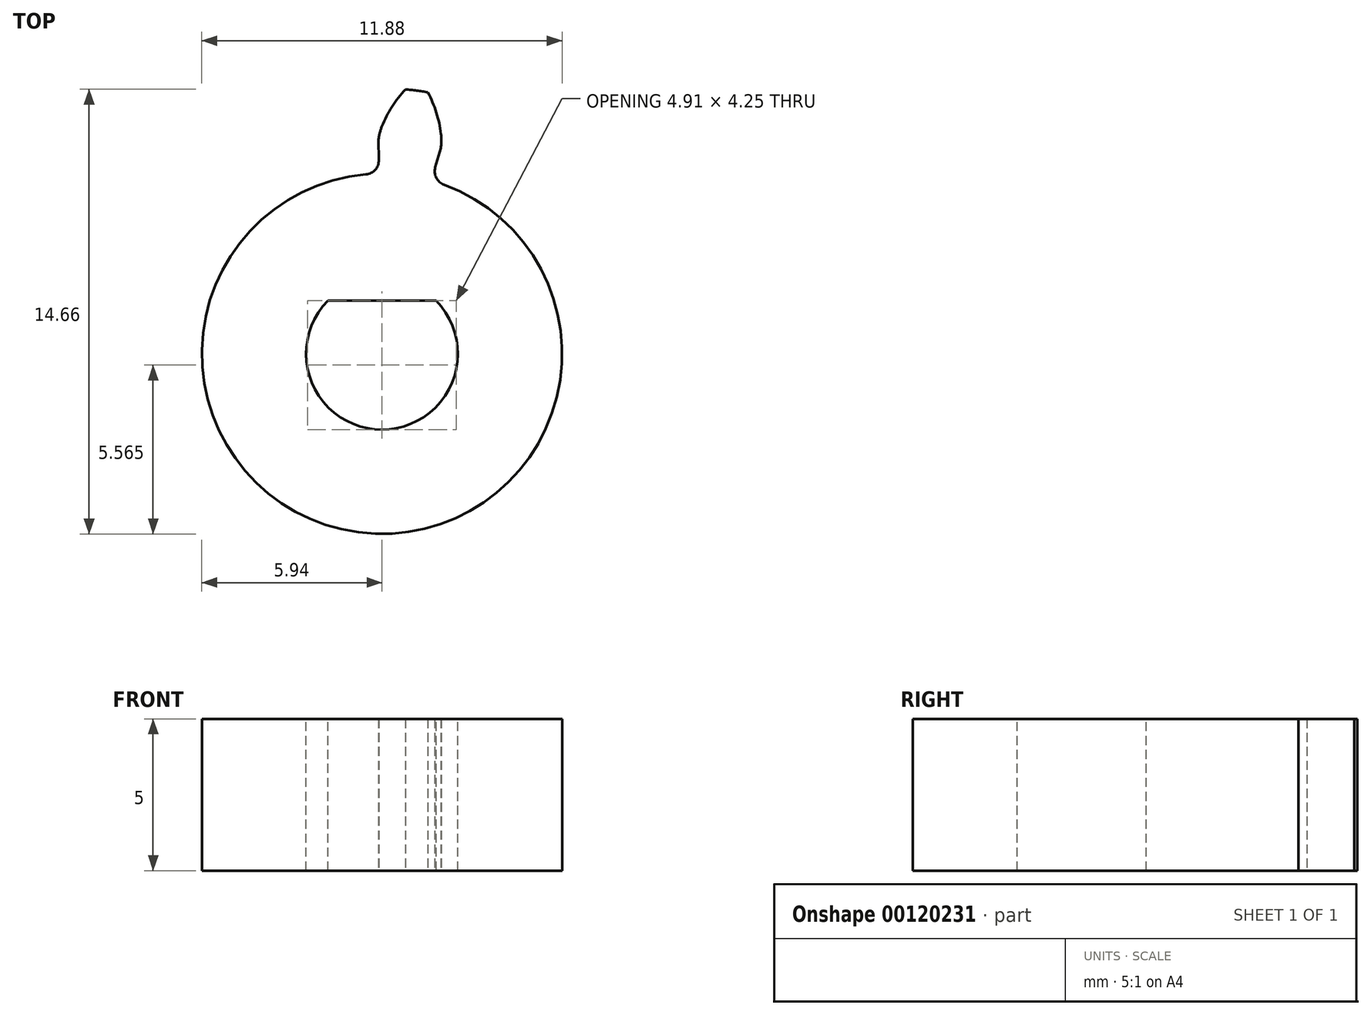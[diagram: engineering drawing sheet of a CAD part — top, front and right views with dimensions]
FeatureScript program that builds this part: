
annotation { "Feature Type Name" : "Feature", "Feature Type Description" : "" }
export const myFeature = defineFeature(function(context is Context, id is Id, definition is map)
    precondition{}
    {
        {
            var Q0;
            Q0=qCreatedBy(makeId("Front.planeOp"),FACE);
            var sketch = newSketch(context, id + "F0", { "sketchPlane" : qUnion([Q0])});
            skLineSegment(sketch, "E0", {"start": v(0, 72.27) * mm, "end": v(0, -50.25) * mm, "construction": true});
            skSolve(sketch);
        }
        {
            var Q0;
            Q0=qCreatedBy(makeId("Top.planeOp"),FACE);
            var sketch = newSketch(context, id + "F1", { "sketchPlane" : qUnion([Q0])});
            skCircle(sketch, "E1", {"center": v(0, 0) * mm, "radius": 7.5 * mm, "construction": true});
            skCircle(sketch, "E2", {"center": v(0, 0) * mm, "radius": 5.94 * mm});
            skSolve(sketch);
        }
        {
            var Q0;
            Q0=qSketchRegion(id+"F1",true);
            extrude(context, id + "F2", {"entities" : qUnion([Q0]), "depth" : 5 * mm});
        }
        {
            var Q0;
            Q0=makeQuery(id+"F2.opExtrude","CAP_FACE",FACE,{"disambiguationData":[OSD([sQuery(id+"F1.wireOp",EDGE,"E2"),sQuery(id+"F1.wireOp",EDGE,"lKhcHiEn-qWT4-b5GR-9CCX-N4hY3lJjeW35"),sQuery(id+"F1.wireOp",EDGE,"zsuhm7zz-1LAn-hH0Z-Fbhr-HMJ1RvOiH2OX")])],"isStart":false});
            var sketch = newSketch(context, id + "F3", { "sketchPlane" : qUnion([Q0])});
            skArc(sketch, "E3", {"start": v(-1.79, 1.75) * mm, "mid": v(0, -2.5) * mm, "end": v(1.79, 1.75) * mm});
            skLineSegment(sketch, "E4", {"start": v(-1.79, 1.75) * mm, "end": v(1.79, 1.75) * mm});
            skPoint(sketch, "E5", {"position": v(0, 2.5) * mm});
            skArc(sketch, "E6", {"start": v(-1.79, 1.75) * mm, "mid": v(0, 2.5) * mm, "end": v(1.79, 1.75) * mm, "construction": true});
            skSolve(sketch);
        }
        {
            var Q0;
            Q0 = qSketchRegion(id + "F3", true);
            extrude(context, id + "F4", {"entities" : qUnion([Q0]), "operationType" : NewBodyOperationType.REMOVE, "endBound" : BoundingType.THROUGH_ALL, "oppositeDirection" : true, "depth" : 25 * mm});
        }
        {
            var Q0;
            Q0=qCreatedBy(makeId("Top.planeOp"),FACE);
            var sketch = newSketch(context, id + "F5", { "sketchPlane" : qUnion([Q0])});
            skLineSegment(sketch, "E7", {"start": v(0, 0) * mm, "end": v(0, 29.7) * mm, "construction": true});
            skLineSegment(sketch, "E8", {"start": v(0, 0) * mm, "end": v(-10.47, 28.76) * mm, "construction": true});
            skLineSegment(sketch, "E9", {"start": v(0, 7.5) * mm, "end": v(-2.41, 6.62) * mm, "construction": true});
            skCircle(sketch, "E10", {"center": v(0, 0) * mm, "radius": 7.5 * mm, "construction": true});
            skCircle(sketch, "E11", {"center": v(0, 0) * mm, "radius": 8.75 * mm, "construction": true});
            skArc(sketch, "E12", {"start": v(-0.53, 5.91) * mm, "mid": v(-0.78, -5.89) * mm, "end": v(2.05, 5.57) * mm, "construction": true});
            skCircle(sketch, "E13", {"center": v(0, 0) * mm, "radius": 7.05 * mm, "construction": true});
            skCircle(sketch, "E14", {"center": v(3.73, 5.98) * mm, "radius": 4.02 * mm, "construction": true});
            skCircle(sketch, "E15", {"center": v(1.5, 6.88) * mm, "radius": 1.63 * mm, "construction": true});
            skArc(sketch, "E16", {"start": v(0.77, 8.72) * mm, "mid": v(0.33, 8.14) * mm, "end": v(0, 7.5) * mm});
            skArc(sketch, "E17", {"start": v(0, 7.5) * mm, "mid": v(-0.07, 7.28) * mm, "end": v(-0.11, 7.05) * mm});
            skLineSegment(sketch, "E18", {"start": v(-0.11, 7.05) * mm, "end": v(-0.1, 6.39) * mm});
            skLineSegment(sketch, "E19", {"start": v(-0.1, 5.94) * mm, "end": v(0, 0) * mm, "construction": true});
            skArc(sketch, "E20", {"start": v(1.95, 7.24) * mm, "mid": v(0.98, 7.44) * mm, "end": v(0, 7.5) * mm});
            skLineSegment(sketch, "E21", {"start": v(0, 0) * mm, "end": v(0.98, 7.44) * mm, "construction": true});
            skLineSegment(sketch, "E22", {"start": v(0.98, 7.44) * mm, "end": v(1.69, 12.76) * mm, "construction": true});
            skArc(sketch, "E23", {"start": v(1.15, 8.67) * mm, "mid": v(0.96, 8.7) * mm, "end": v(0.77, 8.72) * mm});
            skArc(sketch, "E24.MirrorCS", {"start": v(1.15, 8.67) * mm, "mid": v(1.33, 8.65) * mm, "end": v(1.51, 8.62) * mm});
            skArc(sketch, "E25.MirrorCS", {"start": v(1.51, 8.62) * mm, "mid": v(1.8, 7.95) * mm, "end": v(1.95, 7.24) * mm});
            skArc(sketch, "E26.MirrorCS", {"start": v(1.95, 7.24) * mm, "mid": v(1.96, 7) * mm, "end": v(1.94, 6.78) * mm});
            skLineSegment(sketch, "E27.MirrorCS", {"start": v(1.94, 6.78) * mm, "end": v(1.76, 6.14) * mm});
            skPoint(sketch, "E28.visualSharp", {"position": v(-0.1, 5.94) * mm});
            skArc(sketch, "E28.filletArc", {"start": v(-0.53, 5.91) * mm, "mid": v(-0.22, 6.07) * mm, "end": v(-0.1, 6.39) * mm});
            skArc(sketch, "E29.MirrorCS", {"start": v(2.05, 5.57) * mm, "mid": v(1.79, 5.8) * mm, "end": v(1.76, 6.14) * mm});
            skPoint(sketch, "E30.orphan", {"position": v(1.63, 5.7) * mm});
            skArc(sketch, "E31", {"start": v(-0.53, 5.91) * mm, "mid": v(0.78, 5.89) * mm, "end": v(2.05, 5.57) * mm});
            skSolve(sketch);
        }
        {
            var Q0;
            Q0=qSketchRegion(id+"F5",true);
            extrude(context, id + "F6", {"entities" : qUnion([Q0]), "operationType" : NewBodyOperationType.ADD, "depth" : 5 * mm});
        }
    });
